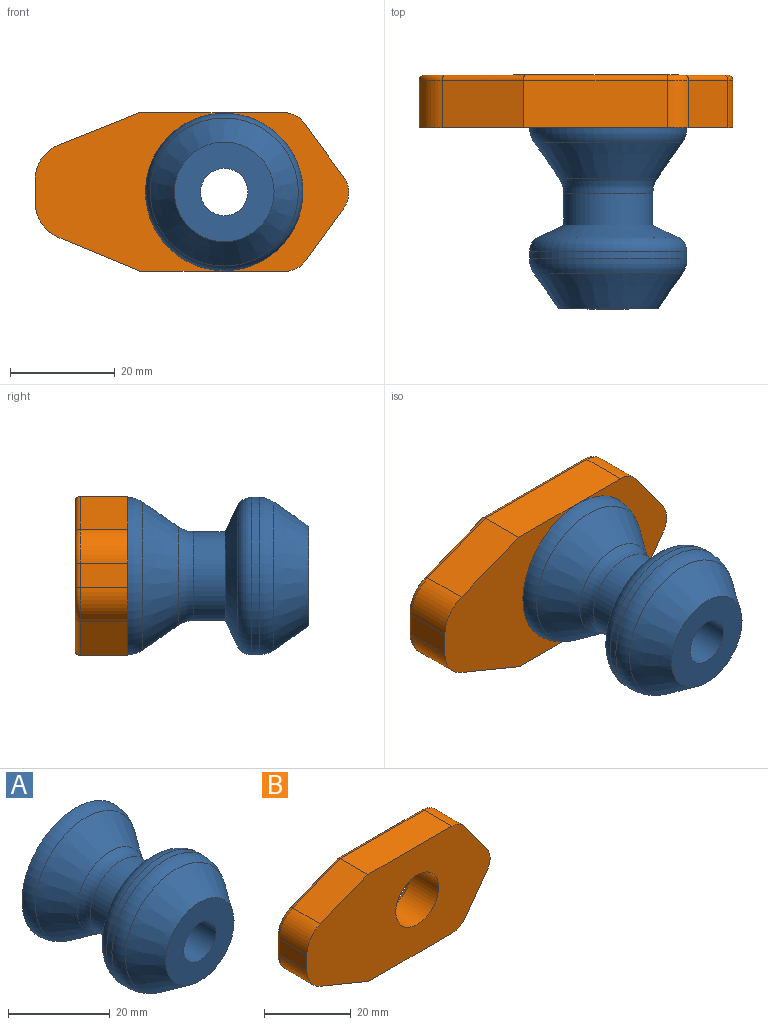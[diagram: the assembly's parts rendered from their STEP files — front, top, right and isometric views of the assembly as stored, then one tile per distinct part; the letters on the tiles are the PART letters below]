
ASSEMBLY  parts=2 mates=1
PART A: 14 faces, bbox 32.5x34.5x32.5 mm
  f0: plane 19x19mm, normal (0,-1,0), area 219.9mm2, adj f1,f13
  f1: cylinder r=4.5mm len=27.73mm, axis (0,-1,0), area 784.1mm2, adj f0,f2
  f2: plane 14x14mm, normal (0,1,0), area 90.3mm2, adj f1,f3
  f3: cylinder r=7mm len=14mm, axis (0,-1,0), area 299.8mm2, adj f2,f4
  f4: plane 30x30mm, normal (0,1,0), area 552.9mm2, adj f3,f5
  f5: torus R=10mm, axis (0,-1,0), area 279.7mm2, adj f4,f6
  f6: cone r=9.37mm half-angle=34.7deg, axis (0,1,0), area 614.3mm2, adj f5,f7
  f7: torus R=13.48mm, axis (0,-1,0), area 167.1mm2, adj f6,f8
  f8: cylinder r=8.48mm len=16.96mm, axis (0,-1,0), area 322.3mm2, adj f7,f9
  f9: cone r=13.29mm half-angle=64.6deg, axis (0,-1,0), area 364.1mm2, adj f8,f10
  f10: torus R=12mm, axis (0,-1,0), area 306mm2, adj f9,f11
  f11: cylinder r=15mm len=30mm, axis (0,-1,0), area 137.6mm2, adj f10,f12
  f12: torus R=10mm, axis (0,-1,0), area 279.7mm2, adj f11,f13
  f13: cone r=9.5mm half-angle=34.7deg, axis (0,1,0), area 600.7mm2, adj f0,f12
PART B: 321 faces, bbox 60.7x10x31.1 mm
  f0: plane 57.74x28.27mm, normal (0,1,0), area 1043.5mm2, adj f15,f16,f17,f18,f19,f20,f21,f22
  f1: cylinder r=7mm len=9mm, axis (0,-1,0), area 75mm2, adj f2,f13,f14,f23
  f2: plane 9x4.58mm, normal (-1,0,0), area 41.2mm2, adj f1,f3,f14,f21
  f3: cylinder r=7mm len=9mm, axis (0,-1,0), area 74.3mm2, adj f2,f4,f14,f19
  f4: plane 15.78x9mm, normal (-0.38,0,-0.92), area 153.7mm2, adj f3,f5,f14,f17
  f5: plane 27.37x9mm, normal (0,0,-1), area 246.4mm2, adj f4,f6,f14,f15
  f6: cylinder r=5mm len=9mm, axis (0,-1,0), area 42.4mm2, adj f5,f7,f14,f16
  f7: plane 9.99x9mm, normal (0.81,0,-0.59), area 111.1mm2, adj f6,f8,f14,f18
  f8: cylinder r=5mm len=9mm, axis (0,-1,0), area 56.5mm2, adj f7,f9,f14,f20
  f9: plane 10.28x9mm, normal (0.81,0,0.59), area 114.4mm2, adj f8,f10,f14,f22
  f10: cylinder r=5mm len=9mm, axis (0,-1,0), area 42.4mm2, adj f9,f11,f14,f24
  f11: plane 27.37x9mm, normal (0,0,1), area 246.4mm2, adj f10,f13,f14,f26
  f12: cylinder r=7mm len=14mm, axis (0,-1,0), area 395.8mm2, adj f14,f27
  f13: plane 15.49x9mm, normal (-0.37,0,0.93), area 150.2mm2, adj f1,f11,f14,f25
  f14: plane 59.74x30.27mm, normal (0,-1,0), area 1348.6mm2, adj f1,f2,f3,f4,f5,f6,f7,f8
  f15: cylinder r=1mm len=27.37mm, axis (-1,0,0), area 42.9mm2, adj f0,f5,f16,f17
  f16: torus R=4mm, axis (0,-1,0), area 6.9mm2, adj f0,f6,f15,f18
  f17: cylinder r=1mm len=16.16mm, axis (-0.92,0,0.38), area 26.7mm2, adj f0,f4,f15,f19
  f18: cylinder r=1mm len=10.57mm, axis (-0.59,0,-0.81), area 19.4mm2, adj f0,f7,f16,f20
  f19: torus R=6mm, axis (0,-1,0), area 12.3mm2, adj f0,f3,f17,f21
  f20: torus R=4mm, axis (0,-1,0), area 9.2mm2, adj f0,f8,f18,f22
  f21: cylinder r=1mm len=4.58mm, axis (0,0,1), area 7.2mm2, adj f0,f2,f19,f23
  f22: cylinder r=1mm len=10.87mm, axis (0.59,0,-0.81), area 20mm2, adj f0,f9,f20,f24
  f23: torus R=6mm, axis (0,-1,0), area 12.4mm2, adj f0,f1,f21,f25
  f24: torus R=4mm, axis (0,-1,0), area 6.9mm2, adj f0,f10,f22,f26
  f25: cylinder r=1mm len=15.87mm, axis (0.93,0,0.37), area 26.1mm2, adj f0,f13,f23,f26
  f26: cylinder r=1mm len=27.37mm, axis (1,0,0), area 42.9mm2, adj f0,f11,f24,f25
  f27: torus R=8mm, axis (0,-1,0), area 72.7mm2, adj f0,f12
  f28: plane 1x0.4mm, normal (0,0,1), area 0.4mm2, adj f0,f29,f31,f32
  f29: plane 3.68x0.4mm, normal (1,0,0), area 1.5mm2, adj f0,f28,f30,f32
  f30: plane 1x0.4mm, normal (0,0,-1), area 0.4mm2, adj f0,f29,f31,f32
  f31: plane 3.68x0.4mm, normal (-1,0,0), area 1.5mm2, adj f0,f28,f30,f32
  f32: plane 3.68x1mm, normal (0,1,0), area 3.7mm2, adj f28,f29,f30,f31
  f33: extruded ~0.9x0.4mm, area 0.4mm2, adj f0,f34,f43,f44
  f34: plane 0.4x0.02mm, normal (0,0,-1), area 0mm2, adj f0,f33,f35,f44
  f35: extruded ~0.48x0.4mm, area 0.2mm2, adj f0,f34,f36,f44
  f36: extruded ~0.42x0.4mm, area 0.2mm2, adj f0,f35,f37,f44
  f37: plane 2.79x0.4mm, normal (1,0,-0.06), area 1.1mm2, adj f0,f36,f38,f44
  f38: plane 0.94x0.4mm, normal (0,0,-1), area 0.4mm2, adj f0,f37,f39,f44
  f39: plane 4.64x0.4mm, normal (-1,0,0.09), area 1.9mm2, adj f0,f38,f40,f44
  f40: plane 1.06x0.4mm, normal (0,0,1), area 0.4mm2, adj f0,f39,f41,f44
  f41: plane 4.64x2.37mm, normal (0.89,0,0.46), area 2.1mm2, adj f0,f40,f42,f44
  f42: plane 1x0.4mm, normal (0,0,-1), area 0.4mm2, adj f0,f41,f43,f44
  f43: plane 2.79x1.37mm, normal (-0.9,0,-0.44), area 1.2mm2, adj f0,f33,f42,f44
  f44: plane 4.64x3.84mm, normal (0,1,0), area 8mm2, adj f33,f34,f35,f36,f37,f38,f39,f40
  f45: extruded ~0.92x0.4mm, area 0.4mm2, adj f0,f46,f67,f68
  f46: extruded ~0.54x0.4mm, area 0.2mm2, adj f0,f45,f47,f68
  f47: extruded ~0.56x0.44mm, area 0.3mm2, adj f0,f46,f48,f68
  f48: extruded ~0.4x0.38mm, area 0.2mm2, adj f0,f47,f49,f68
  f49: extruded ~0.4x0.22mm, area 0.1mm2, adj f0,f48,f50,f68
  f50: extruded ~0.4x0.22mm, area 0.1mm2, adj f0,f49,f51,f68
  f51: extruded ~0.4x0.29mm, area 0.1mm2, adj f0,f50,f52,f68
  f52: extruded ~0.82x0.4mm, area 0.3mm2, adj f0,f51,f53,f68
  f53: plane 0.68x0.4mm, normal (0.91,0,0.42), area 0.3mm2, adj f0,f52,f54,f68
  f54: extruded ~1.15x0.4mm, area 0.5mm2, adj f0,f53,f55,f68
  f55: extruded ~1x0.4mm, area 0.4mm2, adj f0,f54,f56,f68
  f56: extruded ~0.84x0.4mm, area 0.4mm2, adj f0,f55,f57,f68
  f57: extruded ~0.51x0.4mm, area 0.2mm2, adj f0,f56,f58,f68
  f58: extruded ~0.54x0.43mm, area 0.3mm2, adj f0,f57,f59,f68
  f59: extruded ~0.42x0.4mm, area 0.2mm2, adj f0,f58,f60,f68
  f60: extruded ~0.4x0.24mm, area 0.1mm2, adj f0,f59,f61,f68
  f61: extruded ~0.4x0.28mm, area 0.1mm2, adj f0,f60,f62,f68
  f62: extruded ~0.42x0.4mm, area 0.2mm2, adj f0,f61,f63,f68
  f63: extruded ~1.01x0.4mm, area 0.4mm2, adj f0,f62,f64,f68
  f64: plane 0.79x0.4mm, normal (-1,0,0), area 0.3mm2, adj f0,f63,f65,f68
  f65: extruded ~0.47x0.4mm, area 0.2mm2, adj f0,f64,f66,f68
  f66: extruded ~0.59x0.4mm, area 0.2mm2, adj f0,f65,f67,f68
  f67: extruded ~1.1x0.4mm, area 0.5mm2, adj f0,f45,f66,f68
  f68: plane 3.68x2.87mm, normal (0,1,0), area 5.7mm2, adj f45,f46,f47,f48,f49,f50,f51,f52
  f69: extruded ~0.4x0.3mm, area 0.1mm2, adj f0,f70,f80,f81
  f70: extruded ~1.12x0.72mm, area 0.6mm2, adj f0,f69,f71,f81
  f71: plane 0.4x0.02mm, normal (0,0,-1), area 0mm2, adj f0,f70,f72,f81
  f72: plane 0.66x0.4mm, normal (0.99,0,0.1), area 0.3mm2, adj f0,f71,f73,f81
  f73: plane 0.73x0.4mm, normal (0,0,-1), area 0.3mm2, adj f0,f72,f74,f81
  f74: plane 3.55x0.75mm, normal (-0.98,0,-0.21), area 1.5mm2, adj f0,f73,f75,f81
  f75: plane 0.95x0.4mm, normal (0,0,1), area 0.4mm2, adj f0,f74,f76,f81
  f76: plane 1.59x0.4mm, normal (0.98,0,0.21), area 0.6mm2, adj f0,f75,f77,f81
  f77: extruded ~0.83x0.4mm, area 0.4mm2, adj f0,f76,f78,f81
  f78: extruded ~0.65x0.4mm, area 0.3mm2, adj f0,f77,f79,f81
  f79: extruded ~0.4x0.32mm, area 0.1mm2, adj f0,f78,f80,f81
  f80: plane 0.92x0.4mm, normal (0.98,0,0.22), area 0.4mm2, adj f0,f69,f79,f81
  f81: plane 3.61x2.86mm, normal (0,1,0), area 4.4mm2, adj f69,f70,f71,f72,f73,f74,f75,f76
  f82: extruded ~0.55x0.49mm, area 0.3mm2, adj f0,f83,f86,f87
  f83: extruded ~0.55x0.49mm, area 0.3mm2, adj f0,f82,f84,f87
  f84: extruded ~0.41x0.4mm, area 0.2mm2, adj f0,f83,f85,f87
  f85: extruded ~0.4x0.36mm, area 0.2mm2, adj f0,f84,f86,f87
  f86: extruded ~0.55x0.49mm, area 0.3mm2, adj f0,f82,f85,f87
  f87: plane 1.09x0.98mm, normal (0,1,0), area 0.9mm2, adj f82,f83,f84,f85,f86
  f88: plane 0.56x0.44mm, normal (-0.79,0,-0.62), area 0.3mm2, adj f0,f89,f102,f103
  f89: plane 0.4x0.01mm, normal (0,0,-1), area 0mm2, adj f0,f88,f90,f103
  f90: plane 0.84x0.4mm, normal (1,0,0.06), area 0.3mm2, adj f0,f89,f91,f103
  f91: plane 2.28x0.4mm, normal (1,0,0), area 0.9mm2, adj f0,f90,f92,f103
  f92: plane 1x0.4mm, normal (0,0,-1), area 0.4mm2, adj f0,f91,f93,f103
  f93: plane 5.12x0.4mm, normal (-1,0,0), area 2mm2, adj f0,f92,f94,f103
  f94: plane 1x0.4mm, normal (0,0,1), area 0.4mm2, adj f0,f93,f95,f103
  f95: plane 1.15x0.4mm, normal (1,0,0), area 0.5mm2, adj f0,f94,f96,f103
  f96: plane 0.43x0.4mm, normal (0.62,0,0.78), area 0.2mm2, adj f0,f95,f97,f103
  f97: plane 1.49x1.06mm, normal (-0.82,0,0.58), area 0.7mm2, adj f0,f96,f98,f103
  f98: plane 1.16x0.4mm, normal (0,0,1), area 0.5mm2, adj f0,f97,f99,f103
  f99: plane 2.08x1.55mm, normal (0.8,0,-0.6), area 1mm2, adj f0,f98,f100,f103
  f100: plane 1.6x1.46mm, normal (0.74,0,0.68), area 0.9mm2, adj f0,f99,f101,f103
  f101: plane 1.13x0.4mm, normal (0,0,-1), area 0.5mm2, adj f0,f100,f102,f103
  f102: plane 1.12x1.03mm, normal (-0.74,0,-0.68), area 0.6mm2, adj f0,f88,f101,f103
  f103: plane 5.12x3.65mm, normal (0,1,0), area 9.5mm2, adj f88,f89,f90,f91,f92,f93,f94,f95
  f104: extruded ~0.86x0.4mm, area 0.4mm2, adj f0,f105,f129,f130
  f105: extruded ~0.47x0.4mm, area 0.2mm2, adj f0,f104,f106,f130
  f106: extruded ~0.4x0.35mm, area 0.2mm2, adj f0,f105,f107,f130
  f107: extruded ~0.63x0.4mm, area 0.3mm2, adj f0,f106,f108,f130
  f108: extruded ~0.63x0.4mm, area 0.3mm2, adj f0,f107,f109,f130
  f109: extruded ~0.4x0.23mm, area 0.1mm2, adj f0,f108,f110,f130
  f110: extruded ~0.44x0.4mm, area 0.2mm2, adj f0,f109,f111,f130
  f111: extruded ~0.49x0.4mm, area 0.2mm2, adj f0,f110,f112,f130
  f112: extruded ~0.52x0.4mm, area 0.2mm2, adj f0,f111,f113,f130
  f113: plane 0.72x0.4mm, normal (0.92,0,0.39), area 0.3mm2, adj f0,f112,f114,f130
  f114: extruded ~1.29x0.4mm, area 0.5mm2, adj f0,f113,f115,f130
  f115: extruded ~1.08x0.4mm, area 0.5mm2, adj f0,f114,f116,f130
  f116: extruded ~0.76x0.4mm, area 0.4mm2, adj f0,f115,f117,f130
  f117: extruded ~0.48x0.4mm, area 0.2mm2, adj f0,f116,f118,f130
  f118: extruded ~0.4x0.35mm, area 0.2mm2, adj f0,f117,f119,f130
  f119: extruded ~0.62x0.4mm, area 0.3mm2, adj f0,f118,f120,f130
  f120: extruded ~0.47x0.4mm, area 0.2mm2, adj f0,f119,f121,f130
  f121: extruded ~0.4x0.25mm, area 0.1mm2, adj f0,f120,f122,f130
  f122: extruded ~0.4x0.19mm, area 0.1mm2, adj f0,f121,f123,f130
  f123: extruded ~0.55x0.4mm, area 0.3mm2, adj f0,f122,f124,f130
  f124: extruded ~0.62x0.4mm, area 0.3mm2, adj f0,f123,f125,f130
  f125: extruded ~0.63x0.4mm, area 0.3mm2, adj f0,f124,f126,f130
  f126: plane 0.83x0.4mm, normal (-1,0,0), area 0.3mm2, adj f0,f125,f127,f130
  f127: extruded ~0.53x0.4mm, area 0.2mm2, adj f0,f126,f128,f130
  f128: extruded ~0.68x0.4mm, area 0.3mm2, adj f0,f127,f129,f130
  f129: extruded ~1.18x0.4mm, area 0.5mm2, adj f0,f104,f128,f130
  f130: plane 3.81x2.79mm, normal (0,1,0), area 6.8mm2, adj f104,f105,f106,f107,f108,f109,f110,f111
  f131: plane 1.29x0.4mm, normal (-0.98,0,0.21), area 0.5mm2, adj f0,f132,f156,f157
  f132: plane 1.09x0.4mm, normal (0,0,1), area 0.4mm2, adj f0,f131,f133,f157
  f133: plane 3.68x1.06mm, normal (0.96,0,0.28), area 1.5mm2, adj f0,f132,f134,f157
  f134: plane 0.98x0.4mm, normal (0,0,-1), area 0.4mm2, adj f0,f133,f135,f157
  f135: plane 1.63x0.44mm, normal (-0.97,0,-0.26), area 0.7mm2, adj f0,f134,f136,f157
  f136: extruded ~0.56x0.4mm, area 0.2mm2, adj f0,f135,f137,f157
  f137: extruded ~0.65x0.4mm, area 0.3mm2, adj f0,f136,f138,f157
  f138: plane 0.4x0.02mm, normal (0,0,-1), area 0mm2, adj f0,f137,f139,f157
  f139: extruded ~0.4x0.25mm, area 0.1mm2, adj f0,f138,f140,f157
  f140: extruded ~0.4x0.31mm, area 0.1mm2, adj f0,f139,f141,f157
  f141: extruded ~0.4x0.3mm, area 0.1mm2, adj f0,f140,f142,f157
  f142: extruded ~0.4x0.21mm, area 0.1mm2, adj f0,f141,f143,f157
  f143: plane 1.76x0.43mm, normal (0.97,0,-0.24), area 0.7mm2, adj f0,f142,f144,f157
  f144: plane 1.11x0.4mm, normal (0,0,-1), area 0.4mm2, adj f0,f143,f145,f157
  f145: plane 1.76x0.45mm, normal (-0.97,0,-0.25), area 0.7mm2, adj f0,f144,f146,f157
  f146: plane 0.4x0.28mm, normal (-0.98,0,-0.18), area 0.1mm2, adj f0,f145,f147,f157
  f147: extruded ~0.79x0.4mm, area 0.3mm2, adj f0,f146,f148,f157
  f148: plane 0.4x0.02mm, normal (0,0,-1), area 0mm2, adj f0,f147,f149,f157
  f149: extruded ~1.21x0.4mm, area 0.5mm2, adj f0,f148,f150,f157
  f150: plane 1.63x0.42mm, normal (0.97,0,-0.25), area 0.7mm2, adj f0,f149,f151,f157
  f151: plane 1x0.4mm, normal (0,0,-1), area 0.4mm2, adj f0,f150,f152,f157
  f152: plane 3.68x1.05mm, normal (-0.96,0,0.27), area 1.5mm2, adj f0,f151,f153,f157
  f153: plane 1.08x0.4mm, normal (0,0,1), area 0.4mm2, adj f0,f152,f154,f157
  f154: plane 2.91x0.67mm, normal (0.97,0,0.22), area 1.2mm2, adj f0,f153,f155,f157
  f155: plane 0.4x0.02mm, normal (0,0,1), area 0mm2, adj f0,f154,f156,f157
  f156: plane 1.63x0.4mm, normal (-0.97,0,0.23), area 0.7mm2, adj f0,f131,f155,f157
  f157: plane 5.64x3.68mm, normal (0,1,0), area 11.6mm2, adj f131,f132,f133,f134,f135,f136,f137,f138
  f158: extruded ~1.04x0.4mm, area 0.4mm2, adj f0,f159,f181,f182
  f159: extruded ~1.24x0.4mm, area 0.5mm2, adj f0,f158,f160,f182
  f160: plane 0.72x0.4mm, normal (1,0,0), area 0.3mm2, adj f0,f159,f161,f182
  f161: extruded ~0.55x0.4mm, area 0.2mm2, adj f0,f160,f162,f182
  f162: extruded ~0.5x0.4mm, area 0.2mm2, adj f0,f161,f163,f182
  f163: extruded ~0.47x0.4mm, area 0.2mm2, adj f0,f162,f164,f182
  f164: extruded ~0.46x0.4mm, area 0.2mm2, adj f0,f163,f165,f182
  f165: plane 0.4x0.06mm, normal (1,0,0), area 0mm2, adj f0,f164,f166,f182
  f166: plane 0.4x0.07mm, normal (1,0,0.09), area 0mm2, adj f0,f165,f167,f182
  f167: plane 0.4x0.16mm, normal (0,0,1), area 0.1mm2, adj f0,f166,f168,f182
  f168: extruded ~1.51x0.4mm, area 0.6mm2, adj f0,f167,f169,f182
  f169: extruded ~0.91x0.53mm, area 0.4mm2, adj f0,f168,f170,f182
  f170: extruded ~0.71x0.4mm, area 0.3mm2, adj f0,f169,f171,f182
  f171: extruded ~0.88x0.4mm, area 0.4mm2, adj f0,f170,f172,f182
  f172: extruded ~1.01x0.4mm, area 0.4mm2, adj f0,f171,f173,f182
  f173: extruded ~0.83x0.71mm, area 0.4mm2, adj f0,f172,f174,f182
  f174: extruded ~1.2x0.4mm, area 0.5mm2, adj f0,f173,f181,f182
  f175: extruded ~0.53x0.4mm, area 0.2mm2, adj f176,f180,f182,f183
  f176: extruded ~0.4x0.33mm, area 0.2mm2, adj f175,f177,f182,f183
  f177: extruded ~0.42x0.4mm, area 0.2mm2, adj f176,f178,f182,f183
  f178: extruded ~0.77x0.4mm, area 0.3mm2, adj f177,f179,f182,f183
  f179: plane 0.4x0.14mm, normal (0,0,-1), area 0.1mm2, adj f178,f180,f182,f183
  f180: extruded ~0.62x0.4mm, area 0.3mm2, adj f175,f179,f182,f183
  f181: extruded ~1.01x0.4mm, area 0.4mm2, adj f0,f158,f174,f182
  f182: plane 3.68x3.17mm, normal (0,1,0), area 7.1mm2, adj f158,f159,f160,f161,f162,f163,f164,f165
  f183: plane 1.18x0.87mm, normal (0,1,0), area 0.7mm2, adj f175,f176,f177,f178,f179,f180
  f184: plane 0.4x0.39mm, normal (0.04,0,1), area 0.2mm2, adj f185,f208,f209,f318
  f185: plane 0.4x0.3mm, normal (-1,0,0), area 0.1mm2, adj f184,f186,f209,f318
  f186: extruded ~0.53x0.4mm, area 0.2mm2, adj f185,f187,f209,f318
  f187: extruded ~0.56x0.4mm, area 0.2mm2, adj f186,f188,f209,f318
  f188: extruded ~0.49x0.43mm, area 0.3mm2, adj f187,f189,f209,f318
  f189: extruded ~0.44x0.4mm, area 0.2mm2, adj f188,f208,f209,f318
  f190: plane 0.5x0.4mm, normal (-0.93,0,0.36), area 0.2mm2, adj f0,f191,f207,f209
  f191: plane 0.7x0.4mm, normal (0,0,1), area 0.3mm2, adj f0,f190,f192,f209
  f192: plane 2.45x0.4mm, normal (1,0,0), area 1mm2, adj f0,f191,f193,f209
  f193: extruded ~0.98x0.4mm, area 0.4mm2, adj f0,f192,f194,f209
  f194: extruded ~1.14x0.4mm, area 0.5mm2, adj f0,f193,f195,f209
  f195: extruded ~1.41x0.4mm, area 0.6mm2, adj f0,f194,f196,f209
  f196: plane 0.68x0.4mm, normal (-0.9,0,0.44), area 0.3mm2, adj f0,f195,f197,f209
  f197: extruded ~1.04x0.4mm, area 0.4mm2, adj f0,f196,f198,f209
  f198: extruded ~0.57x0.56mm, area 0.4mm2, adj f0,f197,f199,f209
  f199: plane 0.4x0.16mm, normal (-1,0,0), area 0.1mm2, adj f0,f198,f200,f209
  f200: plane 0.64x0.4mm, normal (-0.03,0,-1), area 0.3mm2, adj f0,f199,f201,f209
  f201: extruded ~1.24x0.4mm, area 0.5mm2, adj f0,f200,f202,f209
  f202: extruded ~0.86x0.41mm, area 0.4mm2, adj f0,f201,f203,f209
  f203: extruded ~0.86x0.4mm, area 0.4mm2, adj f0,f202,f204,f209
  f204: extruded ~0.83x0.4mm, area 0.4mm2, adj f0,f203,f205,f209
  f205: extruded ~0.7x0.4mm, area 0.3mm2, adj f0,f204,f206,f209
  f206: extruded ~0.52x0.44mm, area 0.3mm2, adj f0,f205,f207,f209
  f207: plane 0.4x0.03mm, normal (0,0,1), area 0mm2, adj f0,f190,f206,f209
  f208: extruded ~0.65x0.4mm, area 0.3mm2, adj f184,f189,f209,f318
  f209: plane 3.82x3.28mm, normal (0,1,0), area 8.3mm2, adj f184,f185,f186,f187,f188,f189,f190,f191
  f210: plane 0.4x0.39mm, normal (0.04,0,1), area 0.2mm2, adj f211,f234,f235,f319
  f211: plane 0.4x0.3mm, normal (-1,0,0), area 0.1mm2, adj f210,f212,f235,f319
  f212: extruded ~0.53x0.4mm, area 0.2mm2, adj f211,f213,f235,f319
  f213: extruded ~0.56x0.4mm, area 0.2mm2, adj f212,f214,f235,f319
  f214: extruded ~0.49x0.43mm, area 0.3mm2, adj f213,f215,f235,f319
  f215: extruded ~0.44x0.4mm, area 0.2mm2, adj f214,f234,f235,f319
  f216: plane 0.5x0.4mm, normal (-0.93,0,0.36), area 0.2mm2, adj f0,f217,f233,f235
  f217: plane 0.7x0.4mm, normal (0,0,1), area 0.3mm2, adj f0,f216,f218,f235
  f218: plane 2.45x0.4mm, normal (1,0,0), area 1mm2, adj f0,f217,f219,f235
  f219: extruded ~0.98x0.4mm, area 0.4mm2, adj f0,f218,f220,f235
  f220: extruded ~1.14x0.4mm, area 0.5mm2, adj f0,f219,f221,f235
  f221: extruded ~1.41x0.4mm, area 0.6mm2, adj f0,f220,f222,f235
  f222: plane 0.68x0.4mm, normal (-0.9,0,0.44), area 0.3mm2, adj f0,f221,f223,f235
  f223: extruded ~1.04x0.4mm, area 0.4mm2, adj f0,f222,f224,f235
  f224: extruded ~0.57x0.56mm, area 0.4mm2, adj f0,f223,f225,f235
  f225: plane 0.4x0.16mm, normal (-1,0,0), area 0.1mm2, adj f0,f224,f226,f235
  f226: plane 0.64x0.4mm, normal (-0.03,0,-1), area 0.3mm2, adj f0,f225,f227,f235
  f227: extruded ~1.24x0.4mm, area 0.5mm2, adj f0,f226,f228,f235
  f228: extruded ~0.86x0.41mm, area 0.4mm2, adj f0,f227,f229,f235
  f229: extruded ~0.86x0.4mm, area 0.4mm2, adj f0,f228,f230,f235
  f230: extruded ~0.83x0.4mm, area 0.4mm2, adj f0,f229,f231,f235
  f231: extruded ~0.7x0.4mm, area 0.3mm2, adj f0,f230,f232,f235
  f232: extruded ~0.52x0.44mm, area 0.3mm2, adj f0,f231,f233,f235
  f233: plane 0.4x0.03mm, normal (0,0,1), area 0mm2, adj f0,f216,f232,f235
  f234: extruded ~0.65x0.4mm, area 0.3mm2, adj f210,f215,f235,f319
  f235: plane 3.82x3.28mm, normal (0,1,0), area 8.3mm2, adj f210,f211,f212,f213,f214,f215,f216,f217
  f236: plane 0.4x0.39mm, normal (0.04,0,1), area 0.2mm2, adj f237,f260,f261,f320
  f237: plane 0.4x0.3mm, normal (-1,0,0), area 0.1mm2, adj f236,f238,f261,f320
  f238: extruded ~0.53x0.4mm, area 0.2mm2, adj f237,f239,f261,f320
  f239: extruded ~0.56x0.4mm, area 0.2mm2, adj f238,f240,f261,f320
  f240: extruded ~0.49x0.43mm, area 0.3mm2, adj f239,f241,f261,f320
  f241: extruded ~0.44x0.4mm, area 0.2mm2, adj f240,f260,f261,f320
  f242: plane 0.5x0.4mm, normal (-0.93,0,0.36), area 0.2mm2, adj f0,f243,f259,f261
  f243: plane 0.7x0.4mm, normal (0,0,1), area 0.3mm2, adj f0,f242,f244,f261
  f244: plane 2.45x0.4mm, normal (1,0,0), area 1mm2, adj f0,f243,f245,f261
  f245: extruded ~0.98x0.4mm, area 0.4mm2, adj f0,f244,f246,f261
  f246: extruded ~1.14x0.4mm, area 0.5mm2, adj f0,f245,f247,f261
  f247: extruded ~1.41x0.4mm, area 0.6mm2, adj f0,f246,f248,f261
  f248: plane 0.68x0.4mm, normal (-0.9,0,0.44), area 0.3mm2, adj f0,f247,f249,f261
  f249: extruded ~1.04x0.4mm, area 0.4mm2, adj f0,f248,f250,f261
  f250: extruded ~0.57x0.56mm, area 0.4mm2, adj f0,f249,f251,f261
  f251: plane 0.4x0.16mm, normal (-1,0,0), area 0.1mm2, adj f0,f250,f252,f261
  f252: plane 0.64x0.4mm, normal (-0.03,0,-1), area 0.3mm2, adj f0,f251,f253,f261
  f253: extruded ~1.24x0.4mm, area 0.5mm2, adj f0,f252,f254,f261
  f254: extruded ~0.86x0.41mm, area 0.4mm2, adj f0,f253,f255,f261
  f255: extruded ~0.86x0.4mm, area 0.4mm2, adj f0,f254,f256,f261
  f256: extruded ~0.83x0.4mm, area 0.4mm2, adj f0,f255,f257,f261
  f257: extruded ~0.7x0.4mm, area 0.3mm2, adj f0,f256,f258,f261
  f258: extruded ~0.52x0.44mm, area 0.3mm2, adj f0,f257,f259,f261
  f259: plane 0.4x0.03mm, normal (0,0,1), area 0mm2, adj f0,f242,f258,f261
  f260: extruded ~0.65x0.4mm, area 0.3mm2, adj f236,f241,f261,f320
  f261: plane 3.82x3.28mm, normal (0,1,0), area 8.3mm2, adj f236,f237,f238,f239,f240,f241,f242,f243
  f262: plane 0.94x0.4mm, normal (0,0,-1), area 0.4mm2, adj f0,f263,f278,f279
  f263: plane 3.55x0.52mm, normal (-0.99,0,0.14), area 1.4mm2, adj f0,f262,f264,f279
  f264: plane 0.4x0.16mm, normal (-0.88,0,-0.47), area 0.1mm2, adj f0,f263,f265,f279
  f265: extruded ~0.47x0.4mm, area 0.2mm2, adj f0,f264,f266,f279
  f266: extruded ~0.47x0.4mm, area 0.2mm2, adj f0,f265,f267,f279
  f267: extruded ~0.4x0.37mm, area 0.1mm2, adj f0,f266,f268,f279
  f268: plane 0.76x0.4mm, normal (-1,0,0), area 0.3mm2, adj f0,f267,f269,f279
  f269: extruded ~0.47x0.4mm, area 0.2mm2, adj f0,f268,f270,f279
  f270: extruded ~1.53x1.05mm, area 0.8mm2, adj f0,f269,f271,f279
  f271: plane 4.06x2.16mm, normal (0.88,0,0.47), area 1.8mm2, adj f0,f270,f272,f279
  f272: plane 1.04x0.4mm, normal (0,0,-1), area 0.4mm2, adj f0,f271,f273,f279
  f273: plane 1.71x0.82mm, normal (-0.9,0,-0.43), area 0.8mm2, adj f0,f272,f274,f279
  f274: extruded ~0.49x0.4mm, area 0.2mm2, adj f0,f273,f275,f279
  f275: extruded ~0.4x0.38mm, area 0.2mm2, adj f0,f274,f276,f279
  f276: plane 0.4x0.02mm, normal (0,0,-1), area 0mm2, adj f0,f275,f277,f279
  f277: extruded ~0.93x0.4mm, area 0.4mm2, adj f0,f276,f278,f279
  f278: plane 1.64x0.4mm, normal (0.99,0,-0.11), area 0.7mm2, adj f0,f262,f277,f279
  f279: plane 5.11x4.16mm, normal (0,1,0), area 7.9mm2, adj f262,f263,f264,f265,f266,f267,f268,f269
  f280: extruded ~0.92x0.4mm, area 0.4mm2, adj f0,f281,f302,f303
  f281: extruded ~0.54x0.4mm, area 0.2mm2, adj f0,f280,f282,f303
  f282: extruded ~0.56x0.44mm, area 0.3mm2, adj f0,f281,f283,f303
  f283: extruded ~0.4x0.38mm, area 0.2mm2, adj f0,f282,f284,f303
  f284: extruded ~0.4x0.22mm, area 0.1mm2, adj f0,f283,f285,f303
  f285: extruded ~0.4x0.22mm, area 0.1mm2, adj f0,f284,f286,f303
  f286: extruded ~0.4x0.29mm, area 0.1mm2, adj f0,f285,f287,f303
  f287: extruded ~0.82x0.4mm, area 0.3mm2, adj f0,f286,f288,f303
  f288: plane 0.68x0.4mm, normal (0.91,0,0.42), area 0.3mm2, adj f0,f287,f289,f303
  f289: extruded ~1.15x0.4mm, area 0.5mm2, adj f0,f288,f290,f303
  f290: extruded ~1x0.4mm, area 0.4mm2, adj f0,f289,f291,f303
  f291: extruded ~0.84x0.4mm, area 0.4mm2, adj f0,f290,f292,f303
  f292: extruded ~0.51x0.4mm, area 0.2mm2, adj f0,f291,f293,f303
  f293: extruded ~0.54x0.43mm, area 0.3mm2, adj f0,f292,f294,f303
  f294: extruded ~0.42x0.4mm, area 0.2mm2, adj f0,f293,f295,f303
  f295: extruded ~0.4x0.24mm, area 0.1mm2, adj f0,f294,f296,f303
  f296: extruded ~0.4x0.28mm, area 0.1mm2, adj f0,f295,f297,f303
  f297: extruded ~0.42x0.4mm, area 0.2mm2, adj f0,f296,f298,f303
  f298: extruded ~1.01x0.4mm, area 0.4mm2, adj f0,f297,f299,f303
  f299: plane 0.79x0.4mm, normal (-1,0,0), area 0.3mm2, adj f0,f298,f300,f303
  f300: extruded ~0.47x0.4mm, area 0.2mm2, adj f0,f299,f301,f303
  f301: extruded ~0.59x0.4mm, area 0.2mm2, adj f0,f300,f302,f303
  f302: extruded ~1.1x0.4mm, area 0.5mm2, adj f0,f280,f301,f303
  f303: plane 3.68x2.87mm, normal (0,1,0), area 5.7mm2, adj f280,f281,f282,f283,f284,f285,f286,f287
  f304: plane 1.16x0.4mm, normal (0,0,1), area 0.5mm2, adj f0,f305,f316,f317
  f305: plane 2.68x1.69mm, normal (0.85,0,-0.53), area 1.3mm2, adj f0,f304,f306,f317
  f306: plane 2.13x1.68mm, normal (0.79,0,0.62), area 1.1mm2, adj f0,f305,f307,f317
  f307: plane 1.13x0.4mm, normal (0,0,-1), area 0.5mm2, adj f0,f306,f308,f317
  f308: plane 1.64x1.3mm, normal (-0.78,0,-0.62), area 0.8mm2, adj f0,f307,f309,f317
  f309: plane 0.57x0.4mm, normal (-0.82,0,-0.58), area 0.3mm2, adj f0,f308,f310,f317
  f310: plane 2.2x0.4mm, normal (1,0,0), area 0.9mm2, adj f0,f309,f311,f317
  f311: plane 1.02x0.4mm, normal (0,0,-1), area 0.4mm2, adj f0,f310,f312,f317
  f312: plane 4.81x0.4mm, normal (-1,0,0), area 1.9mm2, adj f0,f311,f313,f317
  f313: plane 1.02x0.4mm, normal (0,0,1), area 0.4mm2, adj f0,f312,f314,f317
  f314: plane 1.72x0.4mm, normal (1,0,0), area 0.7mm2, adj f0,f313,f315,f317
  f315: plane 0.43x0.4mm, normal (0.58,0,0.81), area 0.2mm2, adj f0,f314,f316,f317
  f316: plane 2.03x1.26mm, normal (-0.85,0,0.53), area 1mm2, adj f0,f304,f315,f317
  f317: plane 4.81x3.87mm, normal (0,1,0), area 10.6mm2, adj f304,f305,f306,f307,f308,f309,f310,f311
  f318: plane 1.25x1.04mm, normal (0,1,0), area 1.1mm2, adj f184,f185,f186,f187,f188,f189,f208
  f319: plane 1.25x1.04mm, normal (0,1,0), area 1.1mm2, adj f210,f211,f212,f213,f214,f215,f234
  f320: plane 1.25x1.04mm, normal (0,1,0), area 1.1mm2, adj f236,f237,f238,f239,f240,f241,f260
PLACE A t=(1.31,-8.76,-0.92)mm
PLACE B t=(-45.71,3.53,-1.06)mm
MATE fastened B.f12 <-> A.f1  axis (0,-1,0) through (1.31,3.53,-0.92)mm
